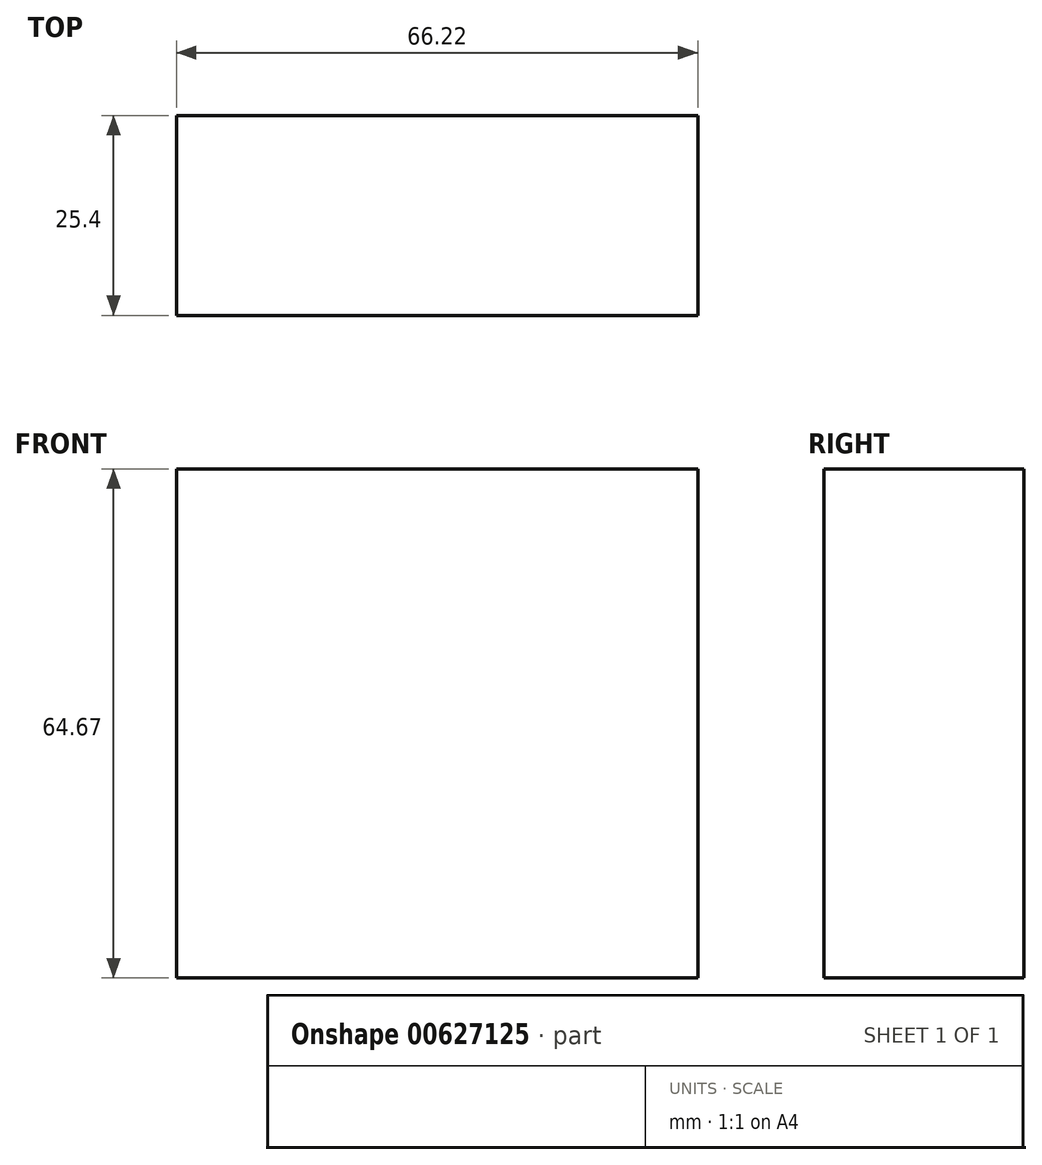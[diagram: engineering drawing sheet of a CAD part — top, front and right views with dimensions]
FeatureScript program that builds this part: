
annotation { "Feature Type Name" : "Feature", "Feature Type Description" : "" }
export const myFeature = defineFeature(function(context is Context, id is Id, definition is map)
    precondition{}
    {
        {
            var Q0;
            Q0=qCreatedBy(makeId("Front.planeOp"),FACE);
            var sketch = newSketch(context, id + "F0", { "sketchPlane" : qUnion([Q0])});
            skLineSegment(sketch, "E0.bottom", {"start": v(-59.38, 64.67) * mm, "end": v(6.84, 64.67) * mm});
            skLineSegment(sketch, "E0.top", {"start": v(-59.38, 0) * mm, "end": v(6.84, 0) * mm});
            skLineSegment(sketch, "E0.left", {"start": v(-59.38, 64.67) * mm, "end": v(-59.38, 0) * mm});
            skLineSegment(sketch, "E0.right", {"start": v(6.84, 64.67) * mm, "end": v(6.84, 0) * mm});
            skSolve(sketch);
        }
        {
            var Q0;
            Q0 = qSketchRegion(id + "F0", true);
            extrude(context, id + "F1", {"entities" : qUnion([Q0]), "depth" : 25.4 * mm, "offsetDistance" : 25.4 * mm});
        }
    });
